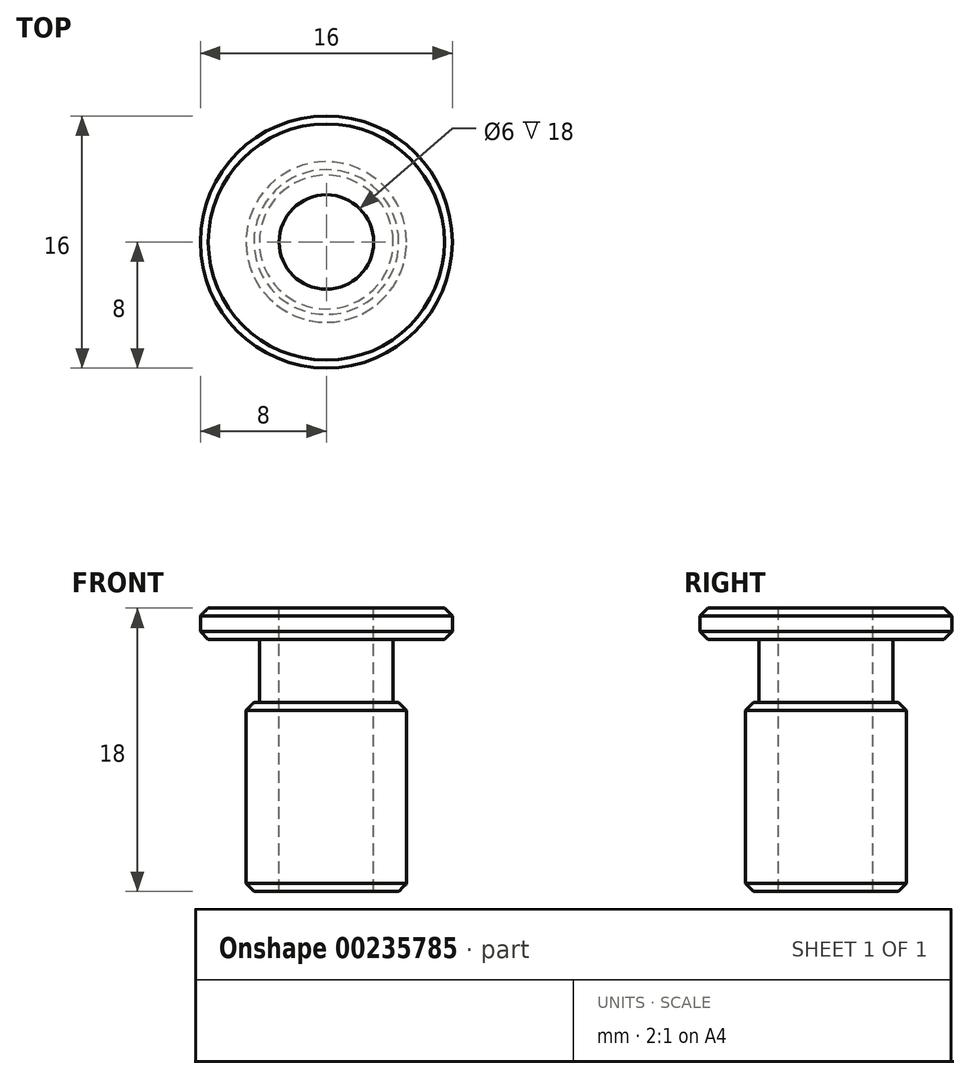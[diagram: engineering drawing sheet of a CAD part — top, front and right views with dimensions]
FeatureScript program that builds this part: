
annotation { "Feature Type Name" : "Feature", "Feature Type Description" : "" }
export const myFeature = defineFeature(function(context is Context, id is Id, definition is map)
    precondition{}
    {
        {
            var Q0;
            Q0=qCreatedBy(makeId("Front.planeOp"),FACE);
            var sketch = newSketch(context, id + "F0", { "sketchPlane" : qUnion([Q0])});
            skLineSegment(sketch, "E0", {"start": v(0, -199.85) * mm, "end": v(8, -199.85) * mm});
            skLineSegment(sketch, "E1", {"start": v(8, -199.85) * mm, "end": v(8, -201.85) * mm});
            skLineSegment(sketch, "E2", {"start": v(8, -201.85) * mm, "end": v(4.25, -201.85) * mm});
            skLineSegment(sketch, "E3", {"start": v(4.25, -201.85) * mm, "end": v(4.25, -205.85) * mm});
            skLineSegment(sketch, "E4", {"start": v(4.25, -205.85) * mm, "end": v(5.1, -205.85) * mm});
            skLineSegment(sketch, "E5", {"start": v(5.1, -205.85) * mm, "end": v(5.1, -217.85) * mm});
            skLineSegment(sketch, "E6", {"start": v(5.1, -217.85) * mm, "end": v(0, -217.85) * mm});
            skLineSegment(sketch, "E7", {"start": v(0, -217.85) * mm, "end": v(0, -199.85) * mm});
            skSolve(sketch);
        }
        {
            var Q0;
            Q0=makeQuery(id+"F0.imprint","IMPRINT",FACE,{"disambiguationData":[TD([[makeQuery(id+"F0.imprint","IMPRINT",EDGE,{"derivedFrom":sQuery(id+"F0.wireOp",EDGE,"E0")}),-1.0]])]});
            var Q1;
            Q1=sQuery(id+"F0.wireOp",EDGE,"E7");
            revolve(context, id + "F1", {"entities" : qUnion([Q0]), "axis" : qUnion([Q1]), "revolveType" : RevolveType.FULL});
        }
        {
            var Q0;
            Q0=makeQuery(id+"F1.opRevolve","SWEPT_EDGE",EDGE,{"disambiguationData":[OSD([sQuery(id+"F0.wireOp",EDGE,"E0"),sQuery(id+"F0.wireOp",EDGE,"E1")])]});
            var Q1;
            Q1=makeQuery(id+"F1.opRevolve","SWEPT_EDGE",EDGE,{"disambiguationData":[OSD([sQuery(id+"F0.wireOp",EDGE,"E1"),sQuery(id+"F0.wireOp",EDGE,"E2")])]});
            var Q2;
            Q2=makeQuery(id+"F1.opRevolve","SWEPT_EDGE",EDGE,{"disambiguationData":[OSD([sQuery(id+"F0.wireOp",EDGE,"E4"),sQuery(id+"F0.wireOp",EDGE,"E5")])]});
            var Q3;
            Q3=makeQuery(id+"F1.opRevolve","SWEPT_EDGE",EDGE,{"disambiguationData":[OSD([sQuery(id+"F0.wireOp",EDGE,"E5"),sQuery(id+"F0.wireOp",EDGE,"E6")])]});
            chamfer(context, id + "F2", {"entities" : qUnion([Q0, Q1, Q2, Q3]), "chamferType" : ChamferType.OFFSET_ANGLE, "width" : .5 * mm, "oppositeDirection" : false, "angle" : 45 * degree, "tangentPropagation" : true});
        }
        {
            var Q0;
            Q0=makeQuery(id+"F1.opRevolve","SWEPT_FACE",FACE,{"disambiguationData":[OSD([sQuery(id+"F0.wireOp",EDGE,"E0")])]});
            var sketch = newSketch(context, id + "F3", { "sketchPlane" : qUnion([Q0])});
            skCircle(sketch, "E8", {"center": v(0, 0) * mm, "radius": 3 * mm});
            skSolve(sketch);
        }
        {
            var Q0;
            Q0=sQuery(id+"F3.wireOp",VERTEX,"E8.center");
            var Q1;
            Q1=makeQuery(id+"F1.opRevolve","SWEPT_BODY",BODY,{"disambiguationData":[OSD([sQuery(id+"F0.wireOp",EDGE,"E0"),sQuery(id+"F0.wireOp",EDGE,"E1"),sQuery(id+"F0.wireOp",EDGE,"E2"),sQuery(id+"F0.wireOp",EDGE,"E3"),sQuery(id+"F0.wireOp",EDGE,"E4"),sQuery(id+"F0.wireOp",EDGE,"E5"),sQuery(id+"F0.wireOp",EDGE,"E6"),sQuery(id+"F0.wireOp",EDGE,"E7")])]});
            hole(context, id + "F4", {"style" : HoleStyle.SIMPLE, "endStyle" : HoleEndStyle.THROUGH, "holeDiameter" : 6 * mm, "locations" : qUnion([Q0]), "scope" : qUnion([Q1]), "isTappedThrough" : true});
        }
    });
